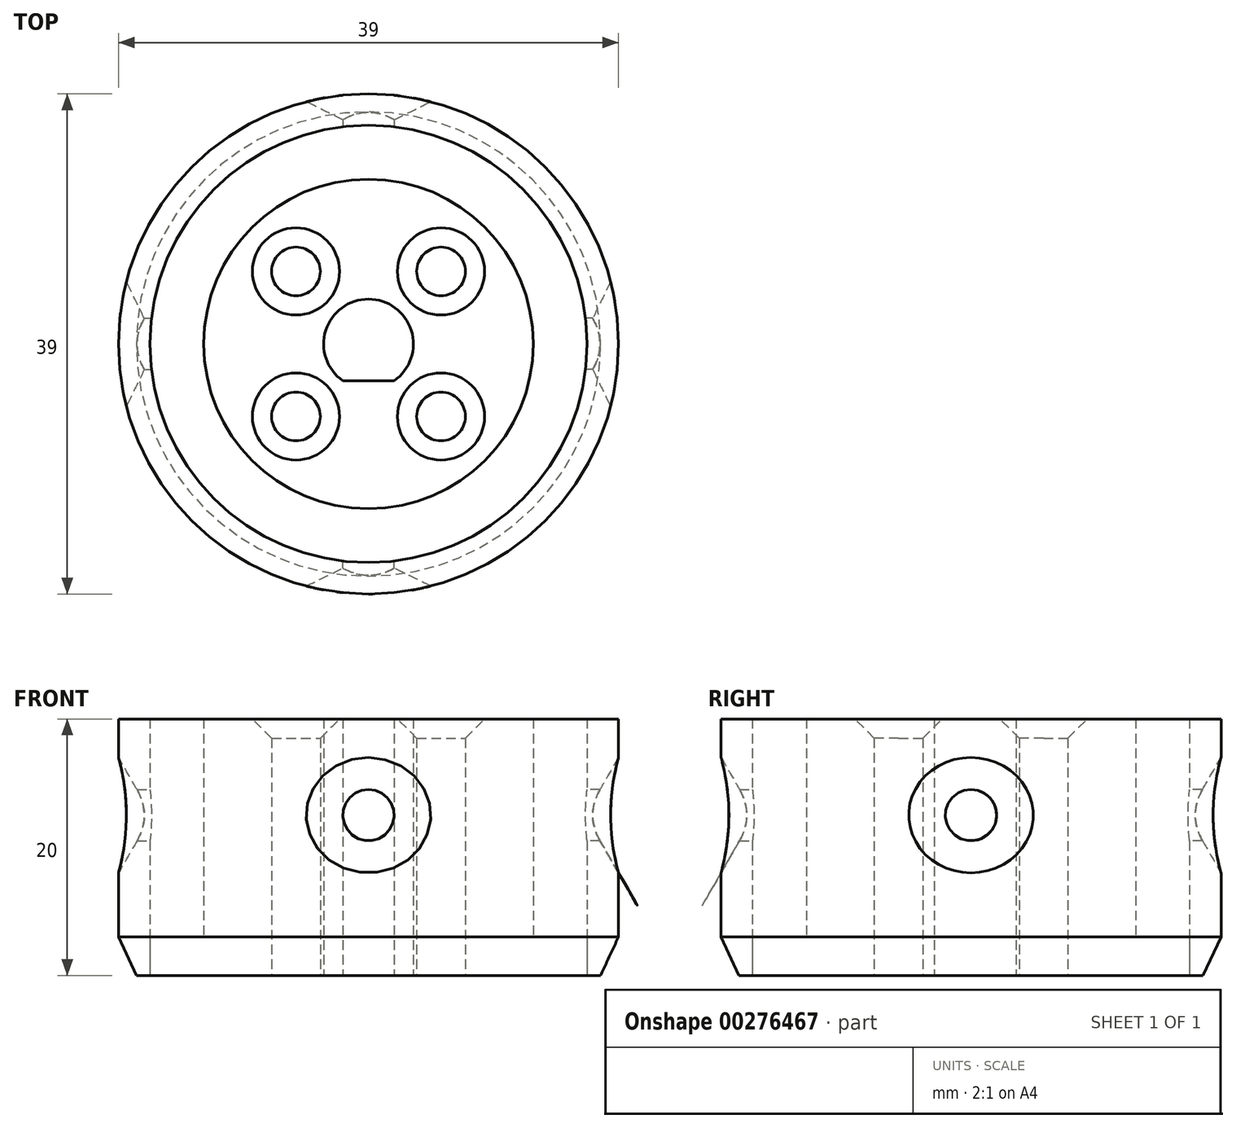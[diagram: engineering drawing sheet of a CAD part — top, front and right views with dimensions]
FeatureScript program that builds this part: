
annotation { "Feature Type Name" : "Feature", "Feature Type Description" : "" }
export const myFeature = defineFeature(function(context is Context, id is Id, definition is map)
    precondition{}
    {
        {
            var Q0;
            Q0=qCreatedBy(makeId("Top.planeOp"),FACE);
            var sketch = newSketch(context, id + "F0", { "sketchPlane" : qUnion([Q0])});
            skCircle(sketch, "E0", {"center": v(0, 0) * mm, "radius": 17.05 * mm});
            skCircle(sketch, "E1", {"center": v(0, 0) * mm, "radius": 3.35 * mm});
            skLineSegment(sketch, "E2", {"start": v(-2.3, -2.44) * mm, "end": v(1.68, -2.9) * mm});
            skSolve(sketch);
        }
        {
            var Q0;
            Q0=makeQuery(id+"F0.imprint","IMPRINT",FACE,{"disambiguationData":[TD([[makeQuery(id+"F0.imprint","IMPRINT",EDGE,{"derivedFrom":sQuery(id+"F0.wireOp",EDGE,"E0")}),1.0]])]});
            var sketch = newSketch(context, id + "F1", { "sketchPlane" : qUnion([Q0])});
            skCircle(sketch, "E3", {"center": v(0, 0) * mm, "radius": 19.5 * mm});
            skSolve(sketch);
        }
        {
            var Q0;
            Q0=makeQuery(id+"F1.imprint","IMPRINT",FACE,{"disambiguationData":[TD([[makeQuery(id+"F1.imprint","IMPRINT",EDGE,{"derivedFrom":sQuery(id+"F1.wireOp",EDGE,"E3")}),1.0]])]});
            var Q1;
            Q1=makeQuery(id+"F0.imprint","IMPRINT",FACE,{"disambiguationData":[TD([[makeQuery(id+"F0.imprint","IMPRINT",EDGE,{"derivedFrom":sQuery(id+"F0.wireOp",EDGE,"E0")}),1.0]])]});
            var Q2;
            {var subQ0=sQuery(id+"F0.wireOp",EDGE,"E2");Q2=makeQuery(id+"F0.imprint","IMPRINT",FACE,{"disambiguationData":[TD([[makeQuery(id+"F0.imprint","IMPRINT",EDGE,{"derivedFrom":subQ0}),1.0]])]});}
            var Q3;
            {var subQ0=sQuery(id+"F0.wireOp",EDGE,"E2");Q3=makeQuery(id+"F0.imprint","IMPRINT",FACE,{"disambiguationData":[TD([[makeQuery(id+"F0.imprint","IMPRINT",EDGE,{"derivedFrom":subQ0}),-1.0]])]});}
            extrude(context, id + "F2", {"entities" : qUnion([Q0, Q1, Q2, Q3]), "depth" : 20 * mm});
        }
        {
            var Q0;
            Q0=makeQuery(id+"F2.opExtrude","CAP_FACE",FACE,{"disambiguationData":[OSD([sQuery(id+"F0.wireOp",EDGE,"E0")])],"isStart":false});
            extrude(context, id + "F3", {"entities" : qUnion([Q0]), "operationType" : NewBodyOperationType.REMOVE, "oppositeDirection" : true, "depth" : 17 * mm});
        }
        {
            var Q0;
            Q0=makeQuery(id+"F2.opExtrude","CAP_FACE",FACE,{"disambiguationData":[OSD([sQuery(id+"F0.wireOp",EDGE,"E0")])],"isStart":true});
            var sketch = newSketch(context, id + "F4", { "sketchPlane" : qUnion([Q0])});
            skCircle(sketch, "E4", {"center": v(0, 0) * mm, "radius": 3.5 * mm});
            skLineSegment(sketch, "E5", {"start": v(-2, 2.87) * mm, "end": v(2, 2.87) * mm});
            skLineSegment(sketch, "E6", {"start": v(3.5, 0) * mm, "end": v(-3.5, 0) * mm, "construction": true});
            skSolve(sketch);
        }
        {
            var Q0;
            {var subQ0=sQuery(id+"F4.wireOp",EDGE,"E5");Q0=makeQuery(id+"F4.imprint","IMPRINT",FACE,{"disambiguationData":[TD([[makeQuery(id+"F4.imprint","IMPRINT",EDGE,{"derivedFrom":subQ0}),-1.0]])]});}
            extrude(context, id + "F5", {"entities" : qUnion([Q0]), "operationType" : NewBodyOperationType.REMOVE, "oppositeDirection" : true, "depth" : 9 * mm});
        }
        {
            var Q0;
            Q0=makeQuery(id+"F2.opExtrude","CAP_FACE",FACE,{"disambiguationData":[OSD([sQuery(id+"F0.wireOp",EDGE,"E0")])],"isStart":true});
            var sketch = newSketch(context, id + "F6", { "sketchPlane" : qUnion([Q0])});
            skLineSegment(sketch, "E7", {"start": v(0, 0) * mm, "end": v(-8, 0) * mm});
            skLineSegment(sketch, "E8", {"start": v(0, 0) * mm, "end": v(0, 8) * mm});
            skLineSegment(sketch, "E9", {"start": v(0, 0) * mm, "end": v(-5.66, 5.66) * mm});
            skLineSegment(sketch, "E10", {"start": v(0, 0) * mm, "end": v(5.66, -5.66) * mm});
            skLineSegment(sketch, "E11", {"start": v(0, 0) * mm, "end": v(-5.66, -5.66) * mm});
            skLineSegment(sketch, "E12", {"start": v(0, 0) * mm, "end": v(5.66, 5.66) * mm});
            skCircle(sketch, "E13", {"center": v(-5.66, 5.66) * mm, "radius": 1.9 * mm});
            skCircle(sketch, "E14", {"center": v(-5.66, -5.66) * mm, "radius": 1.9 * mm});
            skCircle(sketch, "E15", {"center": v(5.66, 5.66) * mm, "radius": 1.9 * mm});
            skCircle(sketch, "E16", {"center": v(5.66, -5.66) * mm, "radius": 1.9 * mm});
            skSolve(sketch);
        }
        {
            var Q0;
            Q0=makeQuery(id+"F6.imprint","IMPRINT",FACE,{"disambiguationData":[TD([[makeQuery(id+"F6.imprint","IMPRINT",EDGE,{"derivedFrom":sQuery(id+"F6.wireOp",EDGE,"E13")}),1.0]])]});
            var Q1;
            Q1=makeQuery(id+"F6.imprint","IMPRINT",FACE,{"disambiguationData":[TD([[makeQuery(id+"F6.imprint","IMPRINT",EDGE,{"derivedFrom":sQuery(id+"F6.wireOp",EDGE,"E14")}),1.0]])]});
            var Q2;
            Q2=makeQuery(id+"F6.imprint","IMPRINT",FACE,{"disambiguationData":[TD([[makeQuery(id+"F6.imprint","IMPRINT",EDGE,{"derivedFrom":sQuery(id+"F6.wireOp",EDGE,"E15")}),1.0]])]});
            var Q3;
            Q3=makeQuery(id+"F6.imprint","IMPRINT",FACE,{"disambiguationData":[TD([[makeQuery(id+"F6.imprint","IMPRINT",EDGE,{"derivedFrom":sQuery(id+"F6.wireOp",EDGE,"E16")}),1.0]])]});
            extrude(context, id + "F7", {"entities" : qUnion([Q0, Q1, Q2, Q3]), "operationType" : NewBodyOperationType.REMOVE, "oppositeDirection" : true, "depth" : 9 * mm});
        }
        {
            var Q0;
            Q0=qCreatedBy(makeId("Front.planeOp"),FACE);
            var sketch = newSketch(context, id + "F8", { "sketchPlane" : qUnion([Q0])});
            skLineSegment(sketch, "E17", {"start": v(0, 0) * mm, "end": v(0, 25) * mm});
            skCircle(sketch, "E18", {"center": v(0, 12.5) * mm, "radius": 2 * mm});
            skSolve(sketch);
        }
        {
            var Q0;
            Q0 = qSketchRegion(id + "F8", true);
            extrude(context, id + "F9", {"entities" : qUnion([Q0]), "operationType" : NewBodyOperationType.REMOVE, "endBound" : BoundingType.THROUGH_ALL, "oppositeDirection" : true, "depth" : 25 * mm});
        }
        {
            var Q0;
            Q0=qCreatedBy(makeId("Front.planeOp"),FACE);
            var sketch = newSketch(context, id + "F10", { "sketchPlane" : qUnion([Q0])});
            skLineSegment(sketch, "E19", {"start": v(0, 0) * mm, "end": v(0, 25) * mm});
            skCircle(sketch, "E20", {"center": v(0, 12.5) * mm, "radius": 2 * mm});
            skSolve(sketch);
        }
        {
            var Q0;
            Q0 = qSketchRegion(id + "F10", true);
            extrude(context, id + "F11", {"entities" : qUnion([Q0]), "operationType" : NewBodyOperationType.REMOVE, "endBound" : BoundingType.THROUGH_ALL, "depth" : 25 * mm});
        }
        {
            var Q0;
            Q0=qCreatedBy(makeId("Right.planeOp"),FACE);
            var sketch = newSketch(context, id + "F12", { "sketchPlane" : qUnion([Q0])});
            skLineSegment(sketch, "E21", {"start": v(0, 0) * mm, "end": v(0, 25) * mm});
            skCircle(sketch, "E22", {"center": v(0, 12.5) * mm, "radius": 2 * mm});
            skSolve(sketch);
        }
        {
            var Q0;
            Q0 = qSketchRegion(id + "F12", true);
            extrude(context, id + "F13", {"entities" : qUnion([Q0]), "operationType" : NewBodyOperationType.REMOVE, "endBound" : BoundingType.THROUGH_ALL, "oppositeDirection" : true, "depth" : 25 * mm});
        }
        {
            var Q0;
            Q0=qCreatedBy(makeId("Right.planeOp"),FACE);
            var sketch = newSketch(context, id + "F14", { "sketchPlane" : qUnion([Q0])});
            skLineSegment(sketch, "E23", {"start": v(0, 0) * mm, "end": v(0, 25) * mm});
            skCircle(sketch, "E24", {"center": v(0, 12.5) * mm, "radius": 2 * mm});
            skSolve(sketch);
        }
        {
            var Q0;
            Q0 = qSketchRegion(id + "F14", true);
            extrude(context, id + "F15", {"entities" : qUnion([Q0]), "operationType" : NewBodyOperationType.REMOVE, "endBound" : BoundingType.THROUGH_ALL, "depth" : 25 * mm});
        }
        {
            var Q0;
            Q0=makeQuery(id+"F3.boolean.opBoolean","COPY",FACE,{"derivedFrom":makeQuery(id+"F3.opExtrude","CAP_FACE",FACE,{"disambiguationData":[OSD([sQuery(id+"F0.wireOp",EDGE,"E0")])],"isStart":false})});
            var sketch = newSketch(context, id + "F16", { "sketchPlane" : qUnion([Q0])});
            skCircle(sketch, "E25", {"center": v(0, 0) * mm, "radius": 12.85 * mm});
            skSolve(sketch);
        }
        {
            var Q0;
            Q0=makeQuery(id+"F16.imprint","IMPRINT",FACE,{"disambiguationData":[TD([[makeQuery(id+"F16.imprint","IMPRINT",EDGE,{"derivedFrom":sQuery(id+"F16.wireOp",EDGE,"E25")}),1.0]])]});
            extrude(context, id + "F17", {"entities" : qUnion([Q0]), "operationType" : NewBodyOperationType.ADD, "depth" : 17 * mm});
        }
        {
            var Q0;
            Q0=makeQuery(id+"F17.opExtrude","CAP_EDGE",EDGE,{"disambiguationData":[OSD([sQuery(id+"F0.wireOp",EDGE,"E0"),sQuery(id+"F6.wireOp",EDGE,"E13")])],"isStart":false});
            var Q1;
            Q1=makeQuery(id+"F17.opExtrude","CAP_EDGE",EDGE,{"disambiguationData":[OSD([sQuery(id+"F0.wireOp",EDGE,"E0"),sQuery(id+"F6.wireOp",EDGE,"E14")])],"isStart":false});
            var Q2;
            Q2=makeQuery(id+"F17.opExtrude","CAP_EDGE",EDGE,{"disambiguationData":[OSD([sQuery(id+"F0.wireOp",EDGE,"E0"),sQuery(id+"F6.wireOp",EDGE,"E16")])],"isStart":false});
            var Q3;
            Q3=makeQuery(id+"F17.opExtrude","CAP_EDGE",EDGE,{"disambiguationData":[OSD([sQuery(id+"F0.wireOp",EDGE,"E0"),sQuery(id+"F6.wireOp",EDGE,"E15")])],"isStart":false});
            chamfer(context, id + "F18", {"entities" : qUnion([Q0, Q1, Q2, Q3]), "width" : 1.5 * mm, "tangentPropagation" : true});
        }
        {
            var Q0;
            Q0=makeQuery(id+"F13.boolean.opBoolean","INTERSECT",EDGE,{"derivedFrom":[makeQuery(id+"F2.opExtrude","SWEPT_FACE",FACE,{"disambiguationData":[OSD([sQuery(id+"F1.wireOp",EDGE,"E3")])]}),makeQuery(id+"F13.opExtrude","SWEPT_FACE",FACE,{"disambiguationData":[OSD([sQuery(id+"F12.wireOp",EDGE,"E22")])]})]});
            var Q1;
            Q1=makeQuery(id+"F9.boolean.opBoolean","INTERSECT",EDGE,{"derivedFrom":[makeQuery(id+"F2.opExtrude","SWEPT_FACE",FACE,{"disambiguationData":[OSD([sQuery(id+"F1.wireOp",EDGE,"E3")])]}),makeQuery(id+"F9.opExtrude","SWEPT_FACE",FACE,{"disambiguationData":[OSD([sQuery(id+"F8.wireOp",EDGE,"E18")])]})]});
            var Q2;
            Q2=makeQuery(id+"F11.boolean.opBoolean","INTERSECT",EDGE,{"derivedFrom":[makeQuery(id+"F2.opExtrude","SWEPT_FACE",FACE,{"disambiguationData":[OSD([sQuery(id+"F1.wireOp",EDGE,"E3")])]}),makeQuery(id+"F11.opExtrude","SWEPT_FACE",FACE,{"disambiguationData":[OSD([sQuery(id+"F10.wireOp",EDGE,"E20")])]})]});
            var Q3;
            Q3=makeQuery(id+"F15.boolean.opBoolean","INTERSECT",EDGE,{"derivedFrom":[makeQuery(id+"F2.opExtrude","SWEPT_FACE",FACE,{"disambiguationData":[OSD([sQuery(id+"F1.wireOp",EDGE,"E3")])]}),makeQuery(id+"F15.opExtrude","SWEPT_FACE",FACE,{"disambiguationData":[OSD([sQuery(id+"F14.wireOp",EDGE,"E24")])]})]});
            chamfer(context, id + "F19", {"entities" : qUnion([Q0, Q1, Q2, Q3]), "chamferType" : ChamferType.OFFSET_ANGLE, "width" : 2.5 * mm, "oppositeDirection" : false, "angle" : 30 * degree, "tangentPropagation" : true});
        }
        {
            var Q0;
            Q0=makeQuery(id+"F2.opExtrude","CAP_EDGE",EDGE,{"disambiguationData":[OSD([sQuery(id+"F1.wireOp",EDGE,"E3")])],"isStart":true});
            chamfer(context, id + "F20", {"entities" : qUnion([Q0]), "chamferType" : ChamferType.OFFSET_ANGLE, "width" : 3 * mm, "oppositeDirection" : false, "angle" : 25 * degree, "tangentPropagation" : true});
        }
    });
